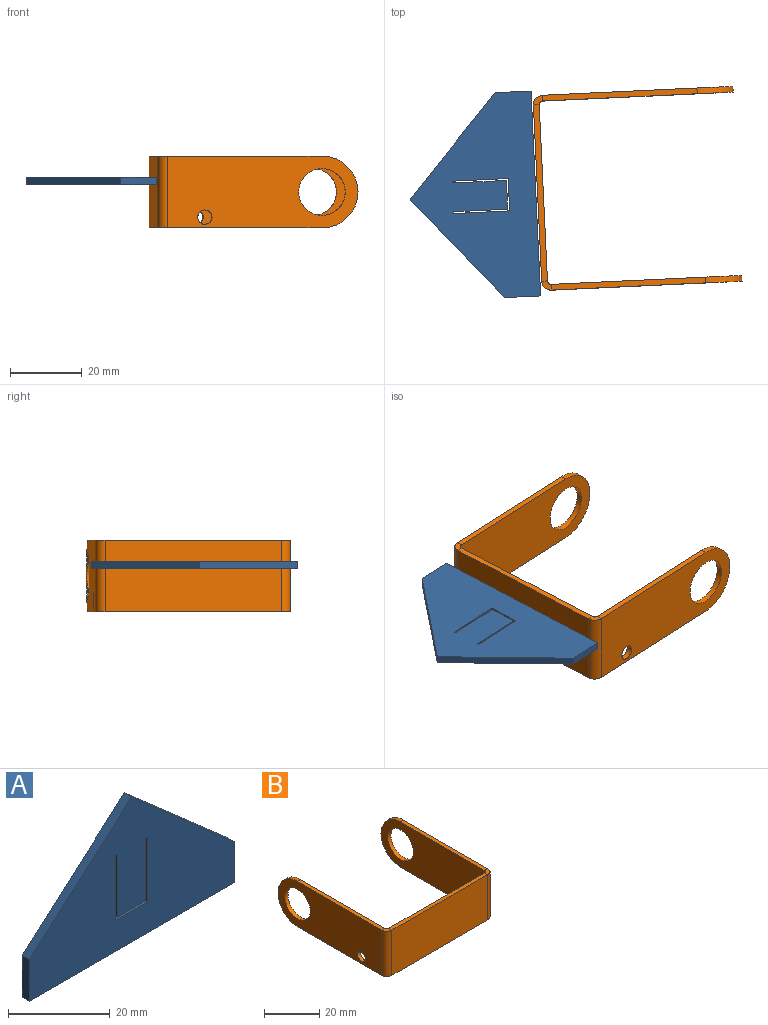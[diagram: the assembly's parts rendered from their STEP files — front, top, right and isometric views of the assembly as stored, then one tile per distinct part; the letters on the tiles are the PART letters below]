
ASSEMBLY  parts=2 mates=1
PART A: 15 faces, bbox 57x2x35 mm
  f0: plane 57x35mm, normal (0,-1,0), area 1263mm2, adj f2,f3,f4,f5,f6,f7,f8,f9
  f1: plane 57x35mm, normal (0,1,0), area 1263mm2, adj f2,f3,f4,f5,f6,f7,f8,f9
  f2: plane 28.5x25mm, normal (-0.66,0,0.75), area 75.8mm2, adj f0,f1,f3,f6
  f3: plane 10x2mm, normal (-1,0,0), area 20mm2, adj f0,f1,f2,f4
  f4: plane 57x2mm, normal (0,0,-1), area 114mm2, adj f0,f1,f3,f5
  f5: plane 10x2mm, normal (1,0,0), area 20mm2, adj f0,f1,f4,f6
  f6: plane 28.5x25mm, normal (0.66,0,0.75), area 75.8mm2, adj f0,f1,f2,f5
  f7: plane 8x2mm, normal (0,0,-1), area 16mm2, adj f0,f1,f8,f14
  f8: plane 15x2mm, normal (-1,0,0), area 30mm2, adj f0,f1,f7,f9
  f9: plane 2x0.5mm, normal (0,0,-1), area 1mm2, adj f0,f1,f8,f10
  f10: plane 15.5x2mm, normal (1,0,0), area 31mm2, adj f0,f1,f9,f11
  f11: plane 9x2mm, normal (0,0,1), area 18mm2, adj f0,f1,f10,f12
  f12: plane 15.5x2mm, normal (-1,0,0), area 31mm2, adj f0,f1,f11,f13
  f13: plane 2x0.5mm, normal (0,0,-1), area 1mm2, adj f0,f1,f12,f14
  f14: plane 15x2mm, normal (1,0,0), area 30mm2, adj f0,f1,f7,f13
PART B: 26 faces, bbox 54.2x55.6x20 mm
  f0: plane 43x1.6mm, normal (0,0,-1), area 68.8mm2, adj f4,f5,f6,f23
  f1: plane 43x1.6mm, normal (0,0,1), area 68.8mm2, adj f4,f5,f6,f22
  f2: cylinder r=6.5mm len=13mm, axis (-1,0,0), area 65.3mm2, adj f4,f5
  f3: cylinder r=2mm len=4mm, axis (-1,0,0), area 20.1mm2, adj f4,f5
  f4: plane 53x20mm, normal (-1,0,0), area 871.8mm2, adj f0,f1,f2,f3,f6,f24
  f5: plane 53x20mm, normal (1,0,0), area 871.8mm2, adj f0,f1,f2,f3,f6,f25
  f6: cylinder r=10mm len=20mm, axis (1,0,0), area 50.3mm2, adj f0,f1,f4,f5
  f7: plane 49x1.6mm, normal (0,0,-1), area 78.4mm2, adj f9,f10,f19,f23
  f8: plane 49x1.6mm, normal (0,0,1), area 78.4mm2, adj f9,f10,f18,f22
  f9: plane 49x20mm, normal (0,-1,0), area 980mm2, adj f7,f8,f20,f24
  f10: plane 49x20mm, normal (0,1,0), area 980mm2, adj f7,f8,f21,f25
  f11: plane 43x1.6mm, normal (0,0,-1), area 68.8mm2, adj f15,f16,f17,f19
  f12: plane 43x1.6mm, normal (0,0,1), area 68.8mm2, adj f15,f16,f17,f18
  f13: cylinder r=6.5mm len=13mm, axis (1,0,0), area 65.3mm2, adj f15,f16
  f14: cylinder r=2mm len=4mm, axis (1,0,0), area 20.1mm2, adj f15,f16
  f15: plane 53x20mm, normal (1,0,0), area 871.8mm2, adj f11,f12,f13,f14,f17,f20
  f16: plane 53x20mm, normal (-1,0,0), area 871.8mm2, adj f11,f12,f13,f14,f17,f21
  f17: cylinder r=10mm len=20mm, axis (-1,0,0), area 50.3mm2, adj f11,f12,f15,f16
  f18: plane 2.6x2.6mm, normal (0,0,1), area 4.5mm2, adj f8,f12,f20,f21
  f19: plane 2.6x2.6mm, normal (0,0,-1), area 4.5mm2, adj f7,f11,f20,f21
  f20: cylinder r=2.6mm len=20mm, axis (0,0,1), area 81.7mm2, adj f9,f15,f18,f19
  f21: cylinder r=1mm len=20mm, axis (0,0,1), area 31.4mm2, adj f10,f16,f18,f19
  f22: plane 2.6x2.6mm, normal (0,0,1), area 4.5mm2, adj f1,f8,f24,f25
  f23: plane 2.6x2.6mm, normal (0,0,-1), area 4.5mm2, adj f0,f7,f24,f25
  f24: cylinder r=2.6mm len=20mm, axis (0,0,1), area 81.7mm2, adj f4,f9,f22,f23
  f25: cylinder r=1mm len=20mm, axis (0,0,1), area 31.4mm2, adj f5,f10,f22,f23
PLACE A rot(axis=(-0.56,-0.59,0.59),121.6deg) t=(-7.19,-10.75,10.97)mm
PLACE B rot(axis=(0,0,-1),87.3deg) t=(38.65,-8.54,8.92)mm
MATE planar B.f9 <-> B.f9  axis (-1,-0.05,0) through (10.78,-9.84,8.92)mm
